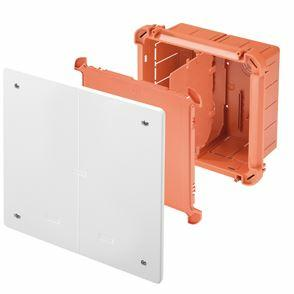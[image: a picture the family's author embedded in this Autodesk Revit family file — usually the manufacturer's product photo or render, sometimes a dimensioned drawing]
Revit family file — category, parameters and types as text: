
# Revit family: Building-FlushMountingEnclosures-GEWISS-48CM-JUNCTION-BOXES_FLUSH-MOUNTING_HIGH_CAPACITY
name_source: partatom
category: Apparecchi elettrici
revit_build: Autodesk Revit 2016 (Build: 20161004_0715(x64)
units: mm (PartAtom-declared; Revit-internal decimal feet)

## family parameters
Condiviso = No
Host = Superficie
Mantenere orientamento annotazione = Sì
Numero OmniClass = 23.80.30.14.24
Punto di calcolo locali = Sì
Quota connettore circolare = Usa diametro
Taglio con vuoti quando caricato = No
Tipo di parte = Normale
Titolo OmniClass = Junction Boxes

## types (2) — shared parameters
Bordo = 4 mm  [stored 0.0131234 ft]
Carico apparente = 0 VA
Catalogue = BUILDING
Catalogue Range = 48 CM
Classificazione = Other
Electrocod = 0220
For walls = Masonry
GEWISS SCHEDA TECNICA = http://pro.gewiss.com
Glow Wire Test = 650°C
IDF = 623b033f-7a9b-4e58-b226-af40efa56f5e
IDT = 14496fa0-f6cd-4977-b717-7ad3c308566f
IP degree = IP40
Immagine tipo = 48CM.JPG
Installation = Flush mounting enclosures
Larghezza = 260 mm  [stored 0.853018 ft]
Lid colour = White RAL 9016
Lunghezza = 520 mm  [stored 1.70604 ft]
Operating temperature = -15 ÷ +60°C
Produttore = GEWISS S.p.A.
Profondità = 121 mm  [stored 0.396982 ft]
Prospetto di default = 1219 mm
SEO = Box
Scatola = ROSSO RAL 3000
Shock resistance = IK07
Tappo = GEWISS - BIANCO RAL 9016
Technical sheet = https://www.gewiss.com
Thermo-pressure with ball = 70
Type of material = Halogen-free in compliance with EN 60754-2
URL = https://www.gewiss.com
Version file RFA = 18.0
Voltaggio = 0 V

## per-type parameters (varying)
| type | Compartment pre-arrangement | Descrizione | Dispersible max power (W) | Dispersible power (W) | EAN code | Modello | Outer dim. LxHxD (mm) |
| GW48211 - UPRIGHTS BOX 520X260X121 PLAIN LID | 5 | UPRIGHTS BOX 520X260X121 PLAIN LID | 30 | 30 | 8011564027299 | GW48211 | 520x260x121 |
| GW48207 - UPRIGHTS BOX 260X260X121 PLAIN LID | 2 | UPRIGHTS BOX 260X260X121 PLAIN LID | 13 | 13 | 8011564027282 | GW48207 | 260x260x121 |

note: source unit labels omitted for Thermo-pressure with ball — the stored unit's dimension contradicts the parameter name (converter mislabeling)

note: [stored X ft] marks values corroborated as IEEE doubles in the binary element streams (Revit-internal decimal feet)

## geometry (parser evidence)
native form markers: Blend x2, Sweep x1
no freeform markers — native parametric forms only
